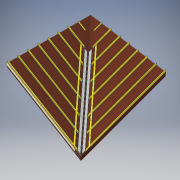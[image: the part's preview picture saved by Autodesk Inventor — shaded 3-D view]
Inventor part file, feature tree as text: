
AUTODESK INVENTOR PART (.ipt)
format: ipt  version: 2019 (Build 230136000, 136)  size: 3,204,608 bytes
history: native  units: in
note: dims shown in document units (in); Inventor stores cm internally (conversion verified against a paired STEP export)
features: plane x11, sketch x10, extrude x6, mirror x5, sweep x1
ambient origin geometry x8: Origin, YZ Plane, XZ Plane, XY Plane, X Axis, Y Axis, Z Axis, Center Point
bodies: Solid1 (feature_tree)
feature tree (33):
  sketch  "Sketch1"  dims[d0=236.2205in d1=236.2205in]
  sketch  "Sketch2"  dims[d2=0.1924in d3=0.213in]
  plane  "Work Plane1"
  plane  "Work Plane2"
  plane  "Work Plane5"
  extrude  "Extrusion1"  Depth=236.2205in
  mirror  "Mirror1"
  plane  "Work Plane6"
  plane  "Work Plane7"
  sketch  "Sketch4"  dims[d4=90.0deg d5=90.0deg]
  extrude  "Extrusion2"  Depth=0.213in
  mirror  "Mirror2"
  plane  "Work Plane14"
  extrude  "Extrusion3"  TaperAngle=90.0deg  [1 undecoded]
  mirror  "Mirror3"
  plane  "Work Plane8"
  plane  "Work Plane9"
  sketch  "Sketch6"  dims[d6=4.7244in d7=0.9843in]
  plane  "Work Plane12"
  extrude  "Extrusion4"  Depth=0.9843in
  mirror  "Mirror4"
  extrude  "Extrusion5"  Depth=0.3937in
  mirror  "Mirror5"
  sketch  "Sketch9"  dims[d19=3.937in d20=0.0in]
  sweep  "Sweep1"
  sketch  "Sketch10"  dims[d21=3.3746in d23=27.5591in d24=0.3937in d26=1.0in]
  extrude  "Extrusion7"  TaperAngle=0.0deg  [1 undecoded]
  plane  "Work Plane3"
  plane  "Work Plane4"
  sketch  "Sketch7"  dims[d8=1.0in d9=0.0in d10=18.1708in d12=5.1181in d13=0.3937in d15=1.0in]
  sketch  "Sketch8"  dims[d17=90.0deg d18=7.874in]
  sketch  "3D Sketch1"
  sketch  "Sketch11"  dims[d28=1.0in d29=0.0in d33=3.1496in d34=0.3937in d35=0.3937in d36=0.9843in d37=1.0in d38=0.0in d39=3.3746in d41=27.5591in d42=0.3937in d44=1.0in d46=90.0deg d47=90.0deg d49=90.0deg d53=3.1496in d54=0.3937in d55=1.5748in d56=236.2205in d57=0.0in d59=0.7874in d61=7.874in d62=0.3937in d64=1.0in d66=7.874in d67=2.7559in d68=2.3622in d69=0.1969in d70=3.3746in d72=27.5591in d73=0.3937in d75=1.0in d77=2.3622in d78=2.7559in d79=0.1969in d88=1.1811in d89=2.7559in d90=20.5566in d91=1.0in d92=0.0in d93=7.874in d95=11.811in d96=0.3937in d98=1.0in d100=0.9843in d104=5.9055in d105=0.0in d106=3.937in d108=0.9843in d111=6.6929in d112=0.9449in d113=6.6929in d114=0.7874in d115=0.0in d116=0.0in d117=15.748in d118=19.685in d123=1.0in d124=0.0in d125=4.3307in d127=9.8425in]
note: 2 required parameter values undecoded (feature->parameter linkage not recoverable at this tier; creation-order binding heuristic only, values carry confidence <= 0.55)
